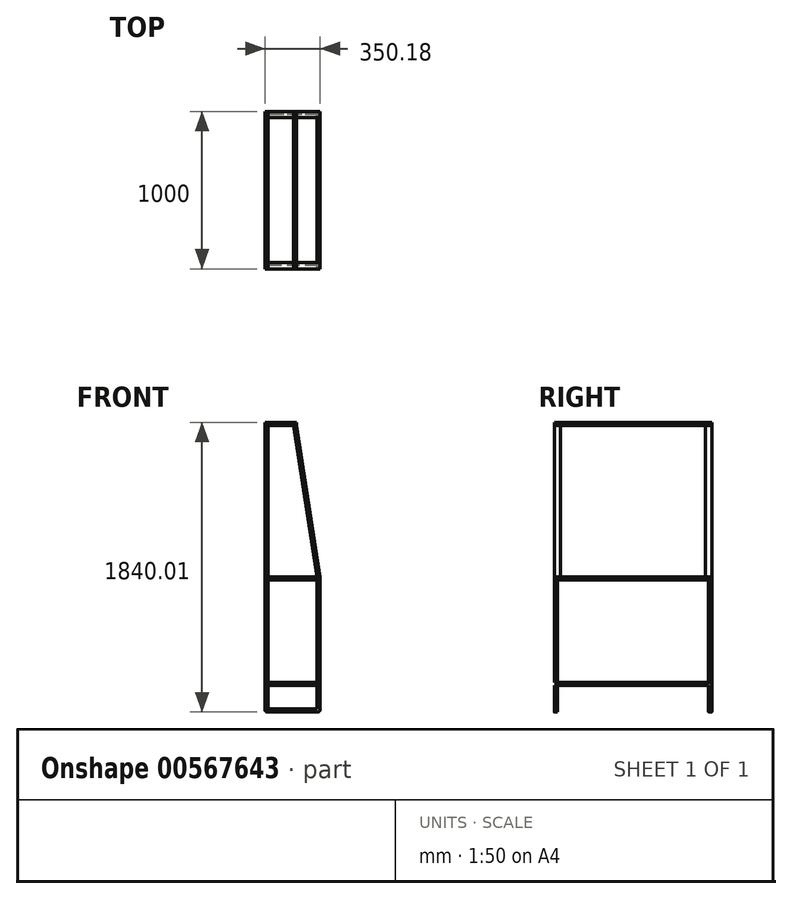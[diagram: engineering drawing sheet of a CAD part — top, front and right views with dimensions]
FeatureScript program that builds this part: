
annotation { "Feature Type Name" : "Feature", "Feature Type Description" : "" }
export const myFeature = defineFeature(function(context is Context, id is Id, definition is map)
    precondition{}
    {
        {
            var Q0;
            Q0=qCreatedBy(makeId("Front.planeOp"),FACE);
            var sketch = newSketch(context, id + "F0", { "sketchPlane" : qUnion([Q0])});
            skLineSegment(sketch, "E0.bottom", {"start": v(0, 0) * mm, "end": v(350, 0) * mm});
            skLineSegment(sketch, "E0.top", {"start": v(0, 1000) * mm, "end": v(200, 1000) * mm});
            skLineSegment(sketch, "E0.left", {"start": v(0, 0) * mm, "end": v(0, 1000) * mm});
            skLineSegment(sketch, "E1", {"start": v(0, 20) * mm, "end": v(350, 20) * mm});
            skLineSegment(sketch, "E2", {"start": v(0, 980) * mm, "end": v(200, 980) * mm});
            skLineSegment(sketch, "E3", {"start": v(200, 980) * mm, "end": v(350, 20) * mm});
            skLineSegment(sketch, "E4", {"start": v(350, 0) * mm, "end": v(350, 20) * mm});
            skLineSegment(sketch, "E5", {"start": v(200, 980) * mm, "end": v(200, 1000) * mm});
            skLineSegment(sketch, "E6", {"start": v(330, 20) * mm, "end": v(330, 0) * mm});
            skLineSegment(sketch, "E7", {"start": v(20, 20) * mm, "end": v(20, 0) * mm});
            skLineSegment(sketch, "E8", {"start": v(180, 980) * mm, "end": v(180, 1000) * mm});
            skLineSegment(sketch, "E9", {"start": v(20, 980) * mm, "end": v(20, 1000) * mm});
            skLineSegment(sketch, "E10", {"start": v(20, 980) * mm, "end": v(20, 20) * mm});
            skLineSegment(sketch, "E11", {"start": v(180, 980) * mm, "end": v(330, 20) * mm});
            skSolve(sketch);
        }
        {
            var Q0;
            {var subQ0=sQuery(id+"F0.wireOp",EDGE,"E5");Q0=makeQuery(id+"F0.imprint","IMPRINT",FACE,{"disambiguationData":[TD([[makeQuery(id+"F0.imprint","IMPRINT",EDGE,{"derivedFrom":subQ0}),1.0]])]});}
            var Q1;
            {var subQ3=sQuery(id+"F0.wireOp",EDGE,"E9");Q1=makeQuery(id+"F0.imprint","IMPRINT",FACE,{"disambiguationData":[TD([[makeQuery(id+"F0.imprint","IMPRINT",EDGE,{"derivedFrom":subQ3}),1.0]])]});}
            var Q2;
            {var subQ3=sQuery(id+"F0.wireOp",EDGE,"E7");Q2=makeQuery(id+"F0.imprint","IMPRINT",FACE,{"disambiguationData":[TD([[makeQuery(id+"F0.imprint","IMPRINT",EDGE,{"derivedFrom":subQ3}),-1.0]])]});}
            var Q3;
            {var subQ0=sQuery(id+"F0.wireOp",EDGE,"E4");Q3=makeQuery(id+"F0.imprint","IMPRINT",FACE,{"disambiguationData":[TD([[makeQuery(id+"F0.imprint","IMPRINT",EDGE,{"derivedFrom":subQ0}),1.0]])]});}
            extrude(context, id + "F1", {"entities" : qUnion([Q0, Q1, Q2, Q3]), "depth" : 1000 * mm, "offsetDistance" : 25 * mm});
        }
        {
            var Q0;
            Q0=makeQuery(id+"F1.opExtrude","CAP_FACE",FACE,{"disambiguationData":[OSD([sQuery(id+"F0.wireOp",EDGE,"E0.top"),sQuery(id+"F0.wireOp",EDGE,"E2"),sQuery(id+"F0.wireOp",EDGE,"E5"),sQuery(id+"F0.wireOp",EDGE,"E8")])],"isStart":false});
            var sketch = newSketch(context, id + "F2", { "sketchPlane" : qUnion([Q0])});
            skLineSegment(sketch, "E12.bottom", {"start": v(-0.05, 0.01) * mm, "end": v(349.95, 0.01) * mm});
            skLineSegment(sketch, "E12.top", {"start": v(-0.05, 1000.01) * mm, "end": v(199.95, 1000.01) * mm});
            skLineSegment(sketch, "E12.left", {"start": v(-0.05, 0.01) * mm, "end": v(-0.05, 1000.01) * mm});
            skLineSegment(sketch, "E13", {"start": v(-0.05, 20.01) * mm, "end": v(349.95, 20.01) * mm});
            skLineSegment(sketch, "E14", {"start": v(-0.05, 980.01) * mm, "end": v(199.95, 980.01) * mm});
            skLineSegment(sketch, "E15", {"start": v(199.95, 980.01) * mm, "end": v(349.95, 20.01) * mm});
            skLineSegment(sketch, "E16", {"start": v(349.95, 0.01) * mm, "end": v(349.95, 20.01) * mm});
            skLineSegment(sketch, "E17", {"start": v(199.95, 980.01) * mm, "end": v(199.95, 1000.01) * mm});
            skLineSegment(sketch, "E18", {"start": v(329.95, 20.01) * mm, "end": v(329.95, 0.01) * mm});
            skLineSegment(sketch, "E19", {"start": v(19.95, 20.01) * mm, "end": v(19.95, 0.01) * mm});
            skLineSegment(sketch, "E20", {"start": v(179.95, 980.01) * mm, "end": v(179.95, 1000.01) * mm});
            skLineSegment(sketch, "E21", {"start": v(19.95, 980.01) * mm, "end": v(19.95, 1000.01) * mm});
            skLineSegment(sketch, "E22", {"start": v(19.95, 980.01) * mm, "end": v(19.95, 20.01) * mm});
            skLineSegment(sketch, "E23", {"start": v(179.95, 980.01) * mm, "end": v(329.95, 20.01) * mm});
            skSolve(sketch);
        }
        {
            var Q0;
            {var subQ0=sQuery(id+"F0.wireOp",EDGE,"E8");Q0=makeQuery(id+"F0.imprint","IMPRINT",FACE,{"disambiguationData":[TD([[makeQuery(id+"F0.imprint","IMPRINT",EDGE,{"derivedFrom":subQ0}),1.0]])]});}
            var Q1;
            {var subQ0=sQuery(id+"F0.wireOp",EDGE,"E3");Q1=makeQuery(id+"F0.imprint","IMPRINT",FACE,{"disambiguationData":[TD([[makeQuery(id+"F0.imprint","IMPRINT",EDGE,{"derivedFrom":subQ0}),-1.0]])]});}
            var Q2;
            {var subQ5=sQuery(id+"F0.wireOp",EDGE,"E10");Q2=makeQuery(id+"F0.imprint","IMPRINT",FACE,{"disambiguationData":[TD([[makeQuery(id+"F0.imprint","IMPRINT",EDGE,{"derivedFrom":subQ5}),-1.0]])]});}
            var Q3;
            {var subQ0=sQuery(id+"F0.wireOp",EDGE,"E6");Q3=makeQuery(id+"F0.imprint","IMPRINT",FACE,{"disambiguationData":[TD([[makeQuery(id+"F0.imprint","IMPRINT",EDGE,{"derivedFrom":subQ0}),-1.0]])]});}
            extrude(context, id + "F3", {"entities" : qUnion([Q0, Q1, Q2, Q3]), "depth" : 40 * mm, "offsetDistance" : 25 * mm});
        }
        {
            var Q0;
            {var subQ5=sQuery(id+"F2.wireOp",EDGE,"E22");Q0=makeQuery(id+"F2.imprint","IMPRINT",FACE,{"disambiguationData":[TD([[makeQuery(id+"F2.imprint","IMPRINT",EDGE,{"derivedFrom":subQ5}),-1.0]])]});}
            var Q1;
            {var subQ0=sQuery(id+"F2.wireOp",EDGE,"E20");Q1=makeQuery(id+"F2.imprint","IMPRINT",FACE,{"disambiguationData":[TD([[makeQuery(id+"F2.imprint","IMPRINT",EDGE,{"derivedFrom":subQ0}),1.0]])]});}
            var Q2;
            {var subQ0=sQuery(id+"F2.wireOp",EDGE,"E15");Q2=makeQuery(id+"F2.imprint","IMPRINT",FACE,{"disambiguationData":[TD([[makeQuery(id+"F2.imprint","IMPRINT",EDGE,{"derivedFrom":subQ0}),-1.0]])]});}
            var Q3;
            {var subQ0=sQuery(id+"F2.wireOp",EDGE,"E18");Q3=makeQuery(id+"F2.imprint","IMPRINT",FACE,{"disambiguationData":[TD([[makeQuery(id+"F2.imprint","IMPRINT",EDGE,{"derivedFrom":subQ0}),-1.0]])]});}
            var Q4;
            {var subQ7=sQuery(id+"F2.wireOp",EDGE,"E23");Q4=makeQuery(id+"F2.imprint","IMPRINT",FACE,{"disambiguationData":[TD([[makeQuery(id+"F2.imprint","IMPRINT",EDGE,{"derivedFrom":subQ7}),1.0]])]});}
            extrude(context, id + "F4", {"entities" : qUnion([Q0, Q1, Q2, Q3, Q4]), "oppositeDirection" : true, "depth" : 40 * mm, "offsetDistance" : 25 * mm});
        }
        {
            var Q0;
            {var subQ0=sQuery(id+"F0.wireOp",EDGE,"E0.bottom");Q0=makeQuery(id+"F1.opExtrude","SWEPT_FACE",FACE,{"disambiguationData":[OSD([subQ0]),TDD([makeQuery(id+"F0.imprint","IMPRINT",EDGE,{"disambiguationData":[TD([[makeQuery(id+"F0.imprint","INTERSECT",VERTEX,{"derivedFrom":[subQ0,sQuery(id+"F0.wireOp",EDGE,"E4")]}),1.0]])],"derivedFrom":subQ0})])]});}
            var sketch = newSketch(context, id + "F5", { "sketchPlane" : qUnion([Q0])});
            skLineSegment(sketch, "E24", {"start": v(350, 0) * mm, "end": v(0, 0) * mm});
            skLineSegment(sketch, "E25", {"start": v(330, 1000) * mm, "end": v(330, 980) * mm});
            skLineSegment(sketch, "E26", {"start": v(330, 980) * mm, "end": v(350, 980) * mm});
            skLineSegment(sketch, "E27", {"start": v(350, 980) * mm, "end": v(350, 1000) * mm});
            skLineSegment(sketch, "E28", {"start": v(330, 20) * mm, "end": v(350, 20) * mm});
            skLineSegment(sketch, "E29.bottom", {"start": v(0, 999.9) * mm, "end": v(20, 999.9) * mm});
            skLineSegment(sketch, "E29.top", {"start": v(0, 979.9) * mm, "end": v(20, 979.9) * mm});
            skLineSegment(sketch, "E29.left", {"start": v(0, 999.9) * mm, "end": v(0, 979.9) * mm});
            skLineSegment(sketch, "E29.right", {"start": v(20, 999.9) * mm, "end": v(20, 979.9) * mm});
            skLineSegment(sketch, "E30", {"start": v(20, 0) * mm, "end": v(0, 0) * mm});
            skLineSegment(sketch, "E31.bottom", {"start": v(0, 0) * mm, "end": v(19.83, 0) * mm});
            skLineSegment(sketch, "E31.top", {"start": v(0, 20) * mm, "end": v(19.83, 20) * mm});
            skLineSegment(sketch, "E31.left", {"start": v(0, 0) * mm, "end": v(0, 20) * mm});
            skLineSegment(sketch, "E31.right", {"start": v(19.83, 0) * mm, "end": v(19.83, 20) * mm});
            skSolve(sketch);
        }
        {
            var Q0;
            Q0=makeQuery(id+"F5.imprint","IMPRINT",FACE,{"disambiguationData":[TD([[makeQuery(id+"F5.imprint","IMPRINT",EDGE,{"derivedFrom":sQuery(id+"F5.wireOp",EDGE,"E29.bottom")}),-1.0]])]});
            var Q1;
            Q1=makeQuery(id+"F5.imprint","IMPRINT",FACE,{"disambiguationData":[TD([[makeQuery(id+"F5.imprint","IMPRINT",EDGE,{"derivedFrom":sQuery(id+"F5.wireOp",EDGE,"E25")}),1.0]])]});
            var Q2;
            {var subQ6=sQuery(id+"F5.wireOp",EDGE,"E28");Q2=makeQuery(id+"F5.imprint","IMPRINT",FACE,{"disambiguationData":[TD([[makeQuery(id+"F5.imprint","IMPRINT",EDGE,{"derivedFrom":subQ6}),-1.0]])]});}
            var Q3;
            Q3=makeQuery(id+"F5.imprint","IMPRINT",FACE,{"disambiguationData":[TD([[makeQuery(id+"F5.imprint","IMPRINT",EDGE,{"derivedFrom":sQuery(id+"F5.wireOp",EDGE,"E31.bottom")}),1.0]])]});
            extrude(context, id + "F6", {"entities" : qUnion([Q0, Q1, Q2, Q3]), "depth" : 650 * mm, "offsetDistance" : 25 * mm});
        }
        {
            var Q0;
            Q0=makeQuery(id+"F6.opExtrude","CAP_FACE",FACE,{"disambiguationData":[OSD([sQuery(id+"F0.wireOp",EDGE,"E0.bottom"),sQuery(id+"F5.wireOp",EDGE,"E25"),sQuery(id+"F5.wireOp",EDGE,"E26"),sQuery(id+"F5.wireOp",EDGE,"E27")])],"isStart":false});
            var sketch = newSketch(context, id + "F7", { "sketchPlane" : qUnion([Q0])});
            skLineSegment(sketch, "E32.bottom", {"start": v(350, 1000) * mm, "end": v(0, 1000) * mm});
            skLineSegment(sketch, "E32.top", {"start": v(350, 0) * mm, "end": v(0, 0) * mm});
            skLineSegment(sketch, "E32.left", {"start": v(350, 1000) * mm, "end": v(350, 0) * mm});
            skLineSegment(sketch, "E32.right", {"start": v(0, 1000) * mm, "end": v(0, 0) * mm});
            skLineSegment(sketch, "E33.bottom", {"start": v(330, 980) * mm, "end": v(20, 980) * mm});
            skLineSegment(sketch, "E33.top", {"start": v(330, 20) * mm, "end": v(20, 20) * mm});
            skLineSegment(sketch, "E33.left", {"start": v(330, 980) * mm, "end": v(330, 20) * mm});
            skLineSegment(sketch, "E33.right", {"start": v(20, 980) * mm, "end": v(20, 20) * mm});
            skLineSegment(sketch, "E34", {"start": v(330, 20) * mm, "end": v(350, 20) * mm});
            skLineSegment(sketch, "E35", {"start": v(20, 20) * mm, "end": v(0, 20) * mm});
            skLineSegment(sketch, "E36", {"start": v(330, 980) * mm, "end": v(350, 980) * mm});
            skLineSegment(sketch, "E37", {"start": v(20, 980) * mm, "end": v(0, 980) * mm});
            skLineSegment(sketch, "E38.bottom", {"start": v(350, 980) * mm, "end": v(0, 980) * mm});
            skLineSegment(sketch, "E38.left", {"start": v(350, 980) * mm, "end": v(350, 1000) * mm});
            skLineSegment(sketch, "E38.right", {"start": v(0, 980) * mm, "end": v(0, 1000) * mm});
            skSolve(sketch);
        }
        {
            var Q0;
            {var subQ0=sQuery(id+"F7.wireOp",EDGE,"E38.right");Q0=makeQuery(id+"F7.imprint","IMPRINT",FACE,{"disambiguationData":[TD([[makeQuery(id+"F7.imprint","IMPRINT",EDGE,{"derivedFrom":subQ0}),-1.0]])]});}
            var Q1;
            {var subQ2=sQuery(id+"F7.wireOp",EDGE,"E38.left");Q1=makeQuery(id+"F7.imprint","IMPRINT",FACE,{"disambiguationData":[TD([[makeQuery(id+"F7.imprint","IMPRINT",EDGE,{"derivedFrom":subQ2}),-1.0]])]});}
            var Q2;
            {var subQ4=sQuery(id+"F7.wireOp",EDGE,"E33.left");Q2=makeQuery(id+"F7.imprint","IMPRINT",FACE,{"disambiguationData":[TD([[makeQuery(id+"F7.imprint","IMPRINT",EDGE,{"derivedFrom":subQ4}),1.0]])]});}
            var Q3;
            {var subQ4=sQuery(id+"F7.wireOp",EDGE,"E33.right");Q3=makeQuery(id+"F7.imprint","IMPRINT",FACE,{"disambiguationData":[TD([[makeQuery(id+"F7.imprint","IMPRINT",EDGE,{"derivedFrom":subQ4}),-1.0]])]});}
            var Q4;
            {var subQ1=sQuery(id+"F7.wireOp",EDGE,"E32.top");Q4=makeQuery(id+"F7.imprint","IMPRINT",FACE,{"disambiguationData":[TD([[makeQuery(id+"F7.imprint","IMPRINT",EDGE,{"derivedFrom":subQ1}),-1.0]])]});}
            extrude(context, id + "F8", {"entities" : qUnion([Q0, Q1, Q2, Q3, Q4]), "depth" : 20 * mm, "offsetDistance" : 25 * mm});
        }
        {
            var Q0;
            Q0=makeQuery(id+"F8.opExtrude","CAP_FACE",FACE,{"disambiguationData":[OSD([sQuery(id+"F7.wireOp",EDGE,"E32.top"),sQuery(id+"F7.wireOp",EDGE,"E32.left"),sQuery(id+"F7.wireOp",EDGE,"E32.right"),sQuery(id+"F7.wireOp",EDGE,"E33.top"),sQuery(id+"F7.wireOp",EDGE,"E33.left"),sQuery(id+"F7.wireOp",EDGE,"E33.right"),sQuery(id+"F7.wireOp",EDGE,"E38.bottom"),sQuery(id+"F7.wireOp",EDGE,"E32.bottom"),sQuery(id+"F7.wireOp",EDGE,"E38.left"),sQuery(id+"F7.wireOp",EDGE,"E38.right")])],"isStart":false});
            var sketch = newSketch(context, id + "F9", { "sketchPlane" : qUnion([Q0])});
            skLineSegment(sketch, "E39.bottom", {"start": v(0, 1000) * mm, "end": v(20, 1000) * mm});
            skLineSegment(sketch, "E39.top", {"start": v(0, 980) * mm, "end": v(20, 980) * mm});
            skLineSegment(sketch, "E39.left", {"start": v(0, 1000) * mm, "end": v(0, 980) * mm});
            skLineSegment(sketch, "E39.right", {"start": v(20, 1000) * mm, "end": v(20, 980) * mm});
            skLineSegment(sketch, "E40.bottom", {"start": v(350, 1000) * mm, "end": v(330, 1000) * mm});
            skLineSegment(sketch, "E40.top", {"start": v(350, 980) * mm, "end": v(330, 980) * mm});
            skLineSegment(sketch, "E40.left", {"start": v(350, 1000) * mm, "end": v(350, 980) * mm});
            skLineSegment(sketch, "E40.right", {"start": v(330, 1000) * mm, "end": v(330, 980) * mm});
            skLineSegment(sketch, "E41.bottom", {"start": v(350, 0) * mm, "end": v(330, 0) * mm});
            skLineSegment(sketch, "E41.top", {"start": v(350, 20) * mm, "end": v(330, 20) * mm});
            skLineSegment(sketch, "E41.left", {"start": v(350, 0) * mm, "end": v(350, 20) * mm});
            skLineSegment(sketch, "E41.right", {"start": v(330, 0) * mm, "end": v(330, 20) * mm});
            skLineSegment(sketch, "E42.bottom", {"start": v(0, 0) * mm, "end": v(20, 0) * mm});
            skLineSegment(sketch, "E42.top", {"start": v(0, 20) * mm, "end": v(20, 20) * mm});
            skLineSegment(sketch, "E42.left", {"start": v(0, 0) * mm, "end": v(0, 20) * mm});
            skLineSegment(sketch, "E42.right", {"start": v(20, 0) * mm, "end": v(20, 20) * mm});
            skSolve(sketch);
        }
        {
            var Q0;
            Q0=makeQuery(id+"F9.imprint","IMPRINT",FACE,{"disambiguationData":[TD([[makeQuery(id+"F9.imprint","IMPRINT",EDGE,{"derivedFrom":sQuery(id+"F9.wireOp",EDGE,"E39.bottom")}),1.0]])]});
            var Q1;
            Q1=makeQuery(id+"F9.imprint","IMPRINT",FACE,{"disambiguationData":[TD([[makeQuery(id+"F9.imprint","IMPRINT",EDGE,{"derivedFrom":sQuery(id+"F9.wireOp",EDGE,"E40.bottom")}),1.0]])]});
            var Q2;
            Q2=makeQuery(id+"F9.imprint","IMPRINT",FACE,{"disambiguationData":[TD([[makeQuery(id+"F9.imprint","IMPRINT",EDGE,{"derivedFrom":sQuery(id+"F9.wireOp",EDGE,"E41.bottom")}),-1.0]])]});
            var Q3;
            Q3=makeQuery(id+"F9.imprint","IMPRINT",FACE,{"disambiguationData":[TD([[makeQuery(id+"F9.imprint","IMPRINT",EDGE,{"derivedFrom":sQuery(id+"F9.wireOp",EDGE,"E42.bottom")}),-1.0]])]});
            extrude(context, id + "F10", {"entities" : qUnion([Q0, Q1, Q2, Q3]), "operationType" : NewBodyOperationType.ADD, "depth" : 150 * mm, "offsetDistance" : 25 * mm});
        }
        {
            var Q0;
            Q0=makeQuery(id+"F10.opExtrude","CAP_FACE",FACE,{"disambiguationData":[OSD([sQuery(id+"F9.wireOp",EDGE,"E40.bottom"),sQuery(id+"F9.wireOp",EDGE,"E40.top"),sQuery(id+"F9.wireOp",EDGE,"E40.left"),sQuery(id+"F9.wireOp",EDGE,"E40.right")])],"isStart":false});
            var sketch = newSketch(context, id + "F11", { "sketchPlane" : qUnion([Q0])});
            skLineSegment(sketch, "E43", {"start": v(350, 980) * mm, "end": v(0, 980) * mm});
            skLineSegment(sketch, "E44", {"start": v(0, 980) * mm, "end": v(0, 1000) * mm});
            skLineSegment(sketch, "E45", {"start": v(0, 1000) * mm, "end": v(350, 1000) * mm});
            skLineSegment(sketch, "E46", {"start": v(350, 1000) * mm, "end": v(350, 980) * mm});
            skLineSegment(sketch, "E47", {"start": v(0, 0) * mm, "end": v(350.13, 0) * mm});
            skLineSegment(sketch, "E48", {"start": v(350.13, 0) * mm, "end": v(350.13, 20.14) * mm});
            skLineSegment(sketch, "E49", {"start": v(350.13, 20.14) * mm, "end": v(0, 20.14) * mm});
            skLineSegment(sketch, "E50", {"start": v(0, 20.14) * mm, "end": v(0, 0) * mm});
            skSolve(sketch);
        }
        {
            var Q0;
            Q0=makeQuery(id+"F11.imprint","IMPRINT",FACE,{"disambiguationData":[TD([[makeQuery(id+"F11.imprint","IMPRINT",EDGE,{"derivedFrom":sQuery(id+"F11.wireOp",EDGE,"E47")}),1.0]])]});
            var Q1;
            {var subQ2=sQuery(id+"F11.wireOp",EDGE,"E44");Q1=makeQuery(id+"F11.imprint","IMPRINT",FACE,{"disambiguationData":[TD([[makeQuery(id+"F11.imprint","IMPRINT",EDGE,{"derivedFrom":subQ2}),-1.0]])]});}
            var Q2;
            {var subQ2=sQuery(id+"F11.wireOp",EDGE,"E46");Q2=makeQuery(id+"F11.imprint","IMPRINT",FACE,{"disambiguationData":[TD([[makeQuery(id+"F11.imprint","IMPRINT",EDGE,{"derivedFrom":subQ2}),-1.0]])]});}
            extrude(context, id + "F12", {"entities" : qUnion([Q0, Q1, Q2]), "operationType" : NewBodyOperationType.ADD, "depth" : 20 * mm, "offsetDistance" : 25 * mm});
        }
        {
            var Q0;
            Q0=makeQuery(id+"F12.opExtrude","CAP_EDGE",EDGE,{"disambiguationData":[OSD([sQuery(id+"F11.wireOp",EDGE,"E46")])],"isStart":false});
            var Q1;
            Q1=makeQuery(id+"F12.opExtrude","CAP_EDGE",EDGE,{"disambiguationData":[OSD([sQuery(id+"F11.wireOp",EDGE,"E44")])],"isStart":false});
            var Q2;
            Q2=makeQuery(id+"F12.opExtrude","CAP_EDGE",EDGE,{"disambiguationData":[OSD([sQuery(id+"F11.wireOp",EDGE,"E50")])],"isStart":false});
            var Q3;
            Q3=makeQuery(id+"F12.opExtrude","CAP_EDGE",EDGE,{"disambiguationData":[OSD([sQuery(id+"F11.wireOp",EDGE,"E48")])],"isStart":false});
            fillet(context, id + "F13", {"entities" : qUnion([Q0, Q1, Q2, Q3]), "radius" : 15 * mm, "tangentPropagation" : true, "allowEdgeOverflow" : false});
        }
    });
